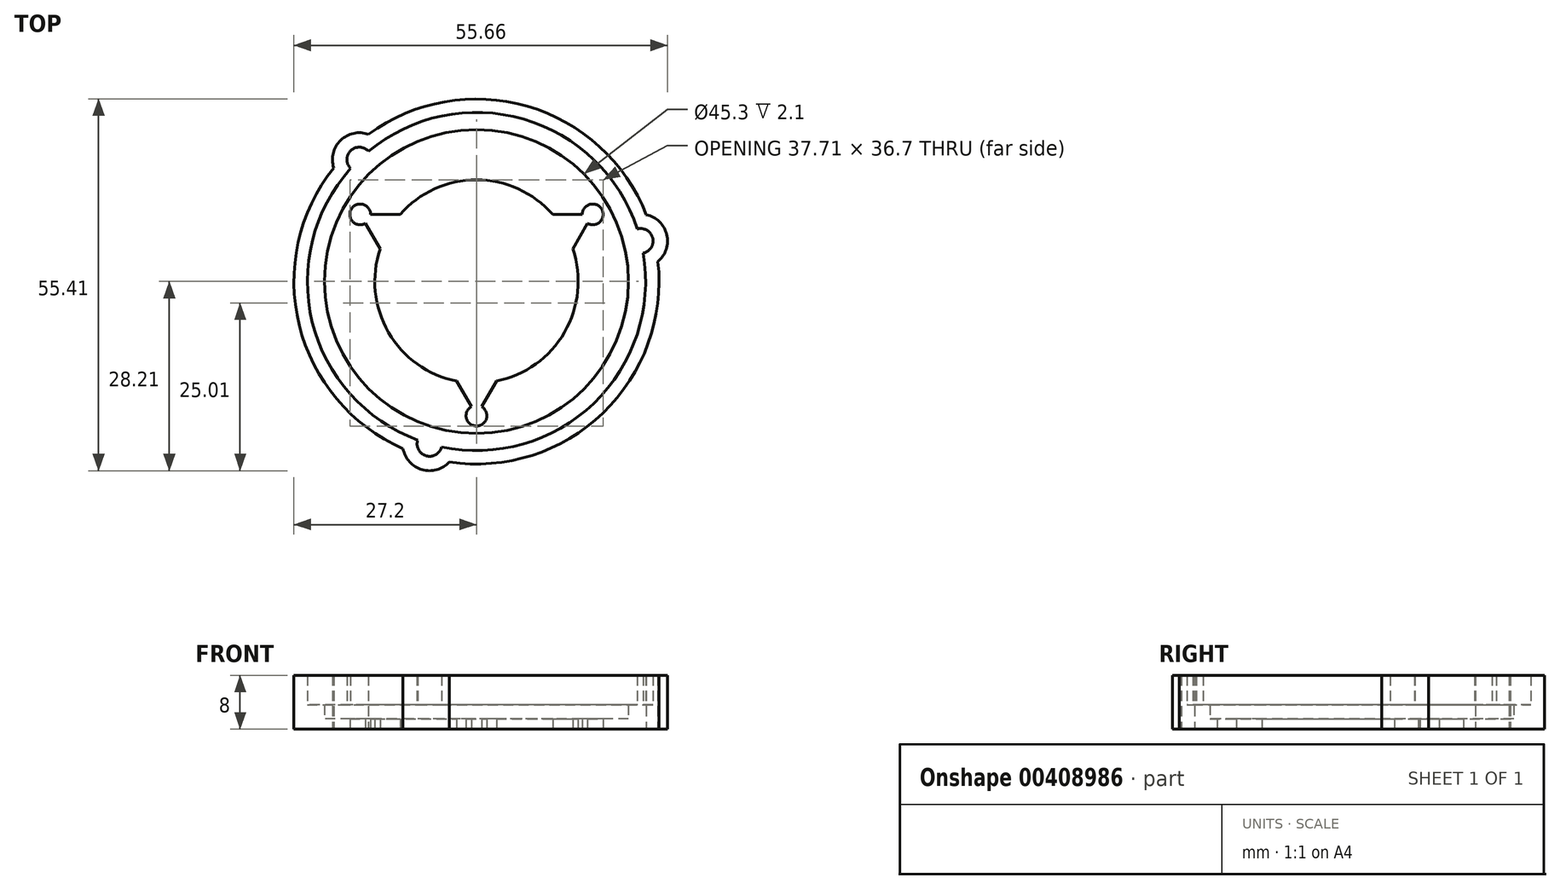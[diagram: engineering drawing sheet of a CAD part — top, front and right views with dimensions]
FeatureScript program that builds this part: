
annotation { "Feature Type Name" : "Feature", "Feature Type Description" : "" }
export const myFeature = defineFeature(function(context is Context, id is Id, definition is map)
    precondition{}
    {
        {
            var Q0;
            Q0=qCreatedBy(makeId("Top.planeOp"),FACE);
            var sketch = newSketch(context, id + "F0", { "sketchPlane" : qUnion([Q0])});
            skCircle(sketch, "E0", {"center": v(0, 0) * mm, "radius": 20 * mm});
            skCircle(sketch, "E1.cCircle", {"center": v(0, 0) * mm, "radius": 20 * mm, "construction": true});
            skCircle(sketch, "E2", {"center": v(0, 0) * mm, "radius": 15.15 * mm});
            skCircle(sketch, "E3", {"center": v(0, 0) * mm, "radius": 0.8 * mm});
            skCircle(sketch, "E4", {"center": v(0, 0) * mm, "radius": 22.65 * mm});
            skCircle(sketch, "E5", {"center": v(0, 0) * mm, "radius": 25.2 * mm});
            skCircle(sketch, "E6", {"center": v(0, 0) * mm, "radius": 27.2 * mm});
            skLineSegment(sketch, "E7.0", {"start": v(0, -20) * mm, "end": v(-17.32, 10) * mm});
            skLineSegment(sketch, "E7.1", {"start": v(-17.32, 10) * mm, "end": v(17.32, 10) * mm});
            skLineSegment(sketch, "E7.2", {"start": v(17.32, 10) * mm, "end": v(0, -20) * mm});
            skCircle(sketch, "E8", {"center": v(-17.32, 10) * mm, "radius": 1.55 * mm});
            skCircle(sketch, "E9", {"center": v(0, -20) * mm, "radius": 1.55 * mm});
            skCircle(sketch, "E10", {"center": v(17.32, 10) * mm, "radius": 1.55 * mm});
            skPoint(sketch, "E11", {"position": v(0, -25.2) * mm});
            skCircle(sketch, "E12.cCircle", {"center": v(0, 0) * mm, "radius": 25.2 * mm, "construction": true});
            skLineSegment(sketch, "E12.0", {"start": v(-7, -24.2) * mm, "end": v(-17.46, 18.17) * mm});
            skLineSegment(sketch, "E12.1", {"start": v(-17.46, 18.17) * mm, "end": v(24.46, 6.04) * mm});
            skLineSegment(sketch, "E12.2", {"start": v(24.46, 6.04) * mm, "end": v(-7, -24.2) * mm});
            skCircle(sketch, "E13", {"center": v(-17.46, 18.17) * mm, "radius": 1.85 * mm});
            skCircle(sketch, "E14", {"center": v(-17.46, 18.17) * mm, "radius": 4 * mm});
            skCircle(sketch, "E15", {"center": v(24.46, 6.04) * mm, "radius": 1.85 * mm});
            skCircle(sketch, "E16", {"center": v(24.46, 6.04) * mm, "radius": 4 * mm});
            skCircle(sketch, "E17", {"center": v(-7, -24.2) * mm, "radius": 1.85 * mm});
            skCircle(sketch, "E18", {"center": v(-7, -24.2) * mm, "radius": 4 * mm});
            skSolve(sketch);
        }
        {
            var Q0;
            Q0 = qSketchRegion(id + "F0", true);
            extrude(context, id + "F1", {"entities" : qUnion([Q0]), "depth" : 8 * mm});
        }
        {
            var Q0;
            {var subQ0=sQuery(id+"F0.wireOp",EDGE,"E14");var subQ1=sQuery(id+"F0.wireOp",EDGE,"E4");var subQ2=makeQuery(id+"F0.imprint","INTERSECT",VERTEX,{"disambiguationData":[OD(1.0)],"derivedFrom":[subQ1,subQ0]});Q0=makeQuery(id+"F0.imprint","IMPRINT",FACE,{"disambiguationData":[TD([[makeQuery(id+"F0.imprint","IMPRINT",EDGE,{"disambiguationData":[TD([[subQ2,-1.0]])],"derivedFrom":subQ1}),-1.0]])]});}
            var Q1;
            {var subQ0=sQuery(id+"F0.wireOp",EDGE,"E12.0");var subQ1=sQuery(id+"F0.wireOp",EDGE,"E4");var subQ2=makeQuery(id+"F0.imprint","INTERSECT",VERTEX,{"disambiguationData":[OD(0.0)],"derivedFrom":[subQ1,subQ0]});Q1=makeQuery(id+"F0.imprint","IMPRINT",FACE,{"disambiguationData":[TD([[makeQuery(id+"F0.imprint","IMPRINT",EDGE,{"disambiguationData":[TD([[subQ2,-1.0]])],"derivedFrom":subQ1}),-1.0]])]});}
            var Q2;
            {var subQ5=sQuery(id+"F0.wireOp",EDGE,"E4");var subQ7=sQuery(id+"F0.wireOp",EDGE,"E14");var subQ9=makeQuery(id+"F0.imprint","INTERSECT",VERTEX,{"disambiguationData":[OD(0.0)],"derivedFrom":[subQ5,subQ7]});Q2=makeQuery(id+"F0.imprint","IMPRINT",FACE,{"disambiguationData":[TD([[makeQuery(id+"F0.imprint","IMPRINT",EDGE,{"disambiguationData":[TD([[subQ9,-1.0]])],"derivedFrom":subQ5}),-1.0]])]});}
            var Q3;
            {var subQ0=sQuery(id+"F0.wireOp",EDGE,"E12.1");var subQ1=sQuery(id+"F0.wireOp",EDGE,"E4");var subQ2=makeQuery(id+"F0.imprint","INTERSECT",VERTEX,{"disambiguationData":[OD(1.0)],"derivedFrom":[subQ1,subQ0]});Q3=makeQuery(id+"F0.imprint","IMPRINT",FACE,{"disambiguationData":[TD([[makeQuery(id+"F0.imprint","IMPRINT",EDGE,{"disambiguationData":[TD([[subQ2,-1.0]])],"derivedFrom":subQ1}),-1.0]])]});}
            var Q4;
            {var subQ1=sQuery(id+"F0.wireOp",EDGE,"E12.0");var subQ3=sQuery(id+"F0.wireOp",EDGE,"E13");var subQ4=makeQuery(id+"F0.imprint","INTERSECT",VERTEX,{"derivedFrom":[subQ1,subQ3]});Q4=makeQuery(id+"F0.imprint","IMPRINT",FACE,{"disambiguationData":[TD([[makeQuery(id+"F0.imprint","IMPRINT",EDGE,{"disambiguationData":[TD([[subQ4,-1.0]])],"derivedFrom":subQ3}),1.0]])]});}
            var Q5;
            {var subQ1=sQuery(id+"F0.wireOp",EDGE,"E5");var subQ3=sQuery(id+"F0.wireOp",EDGE,"E13");var subQ4=makeQuery(id+"F0.imprint","INTERSECT",VERTEX,{"disambiguationData":[OD(1.0)],"derivedFrom":[subQ1,subQ3]});Q5=makeQuery(id+"F0.imprint","IMPRINT",FACE,{"disambiguationData":[TD([[makeQuery(id+"F0.imprint","IMPRINT",EDGE,{"disambiguationData":[TD([[subQ4,-1.0]])],"derivedFrom":subQ3}),1.0]])]});}
            var Q6;
            {var subQ1=sQuery(id+"F0.wireOp",EDGE,"E5");var subQ3=sQuery(id+"F0.wireOp",EDGE,"E13");var subQ4=makeQuery(id+"F0.imprint","INTERSECT",VERTEX,{"disambiguationData":[OD(0.0)],"derivedFrom":[subQ1,subQ3]});Q6=makeQuery(id+"F0.imprint","IMPRINT",FACE,{"disambiguationData":[TD([[makeQuery(id+"F0.imprint","IMPRINT",EDGE,{"disambiguationData":[TD([[subQ4,1.0]])],"derivedFrom":subQ3}),1.0]])]});}
            var Q7;
            {var subQ0=sQuery(id+"F0.wireOp",EDGE,"E5");var subQ2=sQuery(id+"F0.wireOp",EDGE,"E13");var subQ3=makeQuery(id+"F0.imprint","INTERSECT",VERTEX,{"disambiguationData":[OD(0.0)],"derivedFrom":[subQ0,subQ2]});Q7=makeQuery(id+"F0.imprint","IMPRINT",FACE,{"disambiguationData":[TD([[makeQuery(id+"F0.imprint","IMPRINT",EDGE,{"disambiguationData":[TD([[subQ3,-1.0]])],"derivedFrom":subQ2}),1.0]])]});}
            var Q8;
            {var subQ0=sQuery(id+"F0.wireOp",EDGE,"E16");var subQ1=sQuery(id+"F0.wireOp",EDGE,"E4");var subQ2=makeQuery(id+"F0.imprint","INTERSECT",VERTEX,{"disambiguationData":[OD(1.0)],"derivedFrom":[subQ1,subQ0]});Q8=makeQuery(id+"F0.imprint","IMPRINT",FACE,{"disambiguationData":[TD([[makeQuery(id+"F0.imprint","IMPRINT",EDGE,{"disambiguationData":[TD([[subQ2,-1.0]])],"derivedFrom":subQ1}),-1.0]])]});}
            var Q9;
            {var subQ0=sQuery(id+"F0.wireOp",EDGE,"E12.1");var subQ1=sQuery(id+"F0.wireOp",EDGE,"E4");var subQ2=makeQuery(id+"F0.imprint","INTERSECT",VERTEX,{"disambiguationData":[OD(0.0)],"derivedFrom":[subQ1,subQ0]});Q9=makeQuery(id+"F0.imprint","IMPRINT",FACE,{"disambiguationData":[TD([[makeQuery(id+"F0.imprint","IMPRINT",EDGE,{"disambiguationData":[TD([[subQ2,-1.0]])],"derivedFrom":subQ1}),-1.0]])]});}
            var Q10;
            {var subQ1=sQuery(id+"F0.wireOp",EDGE,"E5");var subQ3=sQuery(id+"F0.wireOp",EDGE,"E15");var subQ4=makeQuery(id+"F0.imprint","INTERSECT",VERTEX,{"disambiguationData":[OD(1.0)],"derivedFrom":[subQ1,subQ3]});Q10=makeQuery(id+"F0.imprint","IMPRINT",FACE,{"disambiguationData":[TD([[makeQuery(id+"F0.imprint","IMPRINT",EDGE,{"disambiguationData":[TD([[subQ4,-1.0]])],"derivedFrom":subQ3}),1.0]])]});}
            var Q11;
            {var subQ1=sQuery(id+"F0.wireOp",EDGE,"E12.1");var subQ3=sQuery(id+"F0.wireOp",EDGE,"E15");var subQ4=makeQuery(id+"F0.imprint","INTERSECT",VERTEX,{"derivedFrom":[subQ1,subQ3]});Q11=makeQuery(id+"F0.imprint","IMPRINT",FACE,{"disambiguationData":[TD([[makeQuery(id+"F0.imprint","IMPRINT",EDGE,{"disambiguationData":[TD([[subQ4,-1.0]])],"derivedFrom":subQ3}),1.0]])]});}
            var Q12;
            {var subQ0=sQuery(id+"F0.wireOp",EDGE,"E5");var subQ2=sQuery(id+"F0.wireOp",EDGE,"E15");var subQ3=makeQuery(id+"F0.imprint","INTERSECT",VERTEX,{"disambiguationData":[OD(0.0)],"derivedFrom":[subQ0,subQ2]});Q12=makeQuery(id+"F0.imprint","IMPRINT",FACE,{"disambiguationData":[TD([[makeQuery(id+"F0.imprint","IMPRINT",EDGE,{"disambiguationData":[TD([[subQ3,-1.0]])],"derivedFrom":subQ2}),1.0]])]});}
            var Q13;
            {var subQ0=sQuery(id+"F0.wireOp",EDGE,"E12.2");var subQ1=sQuery(id+"F0.wireOp",EDGE,"E4");var subQ2=makeQuery(id+"F0.imprint","INTERSECT",VERTEX,{"disambiguationData":[OD(0.0)],"derivedFrom":[subQ1,subQ0]});Q13=makeQuery(id+"F0.imprint","IMPRINT",FACE,{"disambiguationData":[TD([[makeQuery(id+"F0.imprint","IMPRINT",EDGE,{"disambiguationData":[TD([[subQ2,-1.0]])],"derivedFrom":subQ1}),-1.0]])]});}
            var Q14;
            {var subQ1=sQuery(id+"F0.wireOp",EDGE,"E5");var subQ3=sQuery(id+"F0.wireOp",EDGE,"E15");var subQ4=makeQuery(id+"F0.imprint","INTERSECT",VERTEX,{"disambiguationData":[OD(0.0)],"derivedFrom":[subQ1,subQ3]});Q14=makeQuery(id+"F0.imprint","IMPRINT",FACE,{"disambiguationData":[TD([[makeQuery(id+"F0.imprint","IMPRINT",EDGE,{"disambiguationData":[TD([[subQ4,1.0]])],"derivedFrom":subQ3}),1.0]])]});}
            var Q15;
            {var subQ3=sQuery(id+"F0.wireOp",EDGE,"E12.2");var subQ5=sQuery(id+"F0.wireOp",EDGE,"E4");var subQ6=makeQuery(id+"F0.imprint","INTERSECT",VERTEX,{"disambiguationData":[OD(0.0)],"derivedFrom":[subQ5,subQ3]});Q15=makeQuery(id+"F0.imprint","IMPRINT",FACE,{"disambiguationData":[TD([[makeQuery(id+"F0.imprint","IMPRINT",EDGE,{"disambiguationData":[TD([[subQ6,1.0]])],"derivedFrom":subQ5}),-1.0]])]});}
            var Q16;
            {var subQ0=sQuery(id+"F0.wireOp",EDGE,"E16");var subQ1=sQuery(id+"F0.wireOp",EDGE,"E4");var subQ2=makeQuery(id+"F0.imprint","INTERSECT",VERTEX,{"disambiguationData":[OD(0.0)],"derivedFrom":[subQ1,subQ0]});Q16=makeQuery(id+"F0.imprint","IMPRINT",FACE,{"disambiguationData":[TD([[makeQuery(id+"F0.imprint","IMPRINT",EDGE,{"disambiguationData":[TD([[subQ2,1.0]])],"derivedFrom":subQ1}),-1.0]])]});}
            var Q17;
            {var subQ3=sQuery(id+"F0.wireOp",EDGE,"E12.2");var subQ5=sQuery(id+"F0.wireOp",EDGE,"E4");var subQ6=makeQuery(id+"F0.imprint","INTERSECT",VERTEX,{"disambiguationData":[OD(1.0)],"derivedFrom":[subQ5,subQ3]});Q17=makeQuery(id+"F0.imprint","IMPRINT",FACE,{"disambiguationData":[TD([[makeQuery(id+"F0.imprint","IMPRINT",EDGE,{"disambiguationData":[TD([[subQ6,-1.0]])],"derivedFrom":subQ5}),-1.0]])]});}
            var Q18;
            {var subQ0=sQuery(id+"F0.wireOp",EDGE,"E12.0");var subQ1=sQuery(id+"F0.wireOp",EDGE,"E4");var subQ2=makeQuery(id+"F0.imprint","INTERSECT",VERTEX,{"disambiguationData":[OD(1.0)],"derivedFrom":[subQ1,subQ0]});Q18=makeQuery(id+"F0.imprint","IMPRINT",FACE,{"disambiguationData":[TD([[makeQuery(id+"F0.imprint","IMPRINT",EDGE,{"disambiguationData":[TD([[subQ2,-1.0]])],"derivedFrom":subQ1}),-1.0]])]});}
            var Q19;
            {var subQ5=sQuery(id+"F0.wireOp",EDGE,"E4");var subQ7=sQuery(id+"F0.wireOp",EDGE,"E18");var subQ9=makeQuery(id+"F0.imprint","INTERSECT",VERTEX,{"disambiguationData":[OD(0.0)],"derivedFrom":[subQ5,subQ7]});Q19=makeQuery(id+"F0.imprint","IMPRINT",FACE,{"disambiguationData":[TD([[makeQuery(id+"F0.imprint","IMPRINT",EDGE,{"disambiguationData":[TD([[subQ9,-1.0]])],"derivedFrom":subQ5}),-1.0]])]});}
            var Q20;
            {var subQ1=sQuery(id+"F0.wireOp",EDGE,"E5");var subQ3=sQuery(id+"F0.wireOp",EDGE,"E17");var subQ4=makeQuery(id+"F0.imprint","INTERSECT",VERTEX,{"disambiguationData":[OD(0.0)],"derivedFrom":[subQ1,subQ3]});Q20=makeQuery(id+"F0.imprint","IMPRINT",FACE,{"disambiguationData":[TD([[makeQuery(id+"F0.imprint","IMPRINT",EDGE,{"disambiguationData":[TD([[subQ4,1.0]])],"derivedFrom":subQ3}),1.0]])]});}
            var Q21;
            {var subQ1=sQuery(id+"F0.wireOp",EDGE,"E12.0");var subQ3=sQuery(id+"F0.wireOp",EDGE,"E17");var subQ4=makeQuery(id+"F0.imprint","INTERSECT",VERTEX,{"derivedFrom":[subQ1,subQ3]});Q21=makeQuery(id+"F0.imprint","IMPRINT",FACE,{"disambiguationData":[TD([[makeQuery(id+"F0.imprint","IMPRINT",EDGE,{"disambiguationData":[TD([[subQ4,1.0]])],"derivedFrom":subQ3}),1.0]])]});}
            var Q22;
            {var subQ1=sQuery(id+"F0.wireOp",EDGE,"E5");var subQ3=sQuery(id+"F0.wireOp",EDGE,"E17");var subQ4=makeQuery(id+"F0.imprint","INTERSECT",VERTEX,{"disambiguationData":[OD(1.0)],"derivedFrom":[subQ1,subQ3]});Q22=makeQuery(id+"F0.imprint","IMPRINT",FACE,{"disambiguationData":[TD([[makeQuery(id+"F0.imprint","IMPRINT",EDGE,{"disambiguationData":[TD([[subQ4,-1.0]])],"derivedFrom":subQ3}),1.0]])]});}
            var Q23;
            {var subQ0=sQuery(id+"F0.wireOp",EDGE,"E5");var subQ2=sQuery(id+"F0.wireOp",EDGE,"E17");var subQ3=makeQuery(id+"F0.imprint","INTERSECT",VERTEX,{"disambiguationData":[OD(0.0)],"derivedFrom":[subQ0,subQ2]});Q23=makeQuery(id+"F0.imprint","IMPRINT",FACE,{"disambiguationData":[TD([[makeQuery(id+"F0.imprint","IMPRINT",EDGE,{"disambiguationData":[TD([[subQ3,-1.0]])],"derivedFrom":subQ2}),1.0]])]});}
            extrude(context, id + "F2", {"entities" : qUnion([Q0, Q1, Q2, Q3, Q4, Q5, Q6, Q7, Q8, Q9, Q10, Q11, Q12, Q13, Q14, Q15, Q16, Q17, Q18, Q19, Q20, Q21, Q22, Q23]), "operationType" : NewBodyOperationType.ADD, "depth" : 3.6 * mm});
        }
        {
            var Q0;
            Q0 = qSketchRegion(id + "F0", true);
            var Q1;
            {var subQ0=sQuery(id+"F0.wireOp",EDGE,"E12.0");var subQ1=sQuery(id+"F0.wireOp",EDGE,"E4");var subQ2=makeQuery(id+"F0.imprint","INTERSECT",VERTEX,{"disambiguationData":[OD(0.0)],"derivedFrom":[subQ1,subQ0]});Q1=makeQuery(id+"F0.imprint","IMPRINT",FACE,{"disambiguationData":[TD([[makeQuery(id+"F0.imprint","IMPRINT",EDGE,{"disambiguationData":[TD([[subQ2,-1.0]])],"derivedFrom":subQ1}),1.0]])]});}
            var Q2;
            {var subQ0=sQuery(id+"F0.wireOp",EDGE,"E12.1");var subQ1=sQuery(id+"F0.wireOp",EDGE,"E4");var subQ2=makeQuery(id+"F0.imprint","INTERSECT",VERTEX,{"disambiguationData":[OD(1.0)],"derivedFrom":[subQ1,subQ0]});Q2=makeQuery(id+"F0.imprint","IMPRINT",FACE,{"disambiguationData":[TD([[makeQuery(id+"F0.imprint","IMPRINT",EDGE,{"disambiguationData":[TD([[subQ2,-1.0]])],"derivedFrom":subQ1}),1.0]])]});}
            var Q3;
            {var subQ0=sQuery(id+"F0.wireOp",EDGE,"E14");var subQ1=sQuery(id+"F0.wireOp",EDGE,"E4");var subQ2=makeQuery(id+"F0.imprint","INTERSECT",VERTEX,{"disambiguationData":[OD(0.0)],"derivedFrom":[subQ1,subQ0]});Q3=makeQuery(id+"F0.imprint","IMPRINT",FACE,{"disambiguationData":[TD([[makeQuery(id+"F0.imprint","IMPRINT",EDGE,{"disambiguationData":[TD([[subQ2,-1.0]])],"derivedFrom":subQ1}),1.0]])]});}
            var Q4;
            {var subQ1=sQuery(id+"F0.wireOp",EDGE,"E0");var subQ4=sQuery(id+"F0.wireOp",EDGE,"E12.1");var subQ11=makeQuery(id+"F0.imprint","INTERSECT",VERTEX,{"disambiguationData":[OD(0.0)],"derivedFrom":[subQ1,subQ4]});Q4=makeQuery(id+"F0.imprint","IMPRINT",FACE,{"disambiguationData":[TD([[makeQuery(id+"F0.imprint","IMPRINT",EDGE,{"disambiguationData":[TD([[subQ11,-1.0]])],"derivedFrom":subQ1}),-1.0]])]});}
            var Q5;
            {var subQ0=sQuery(id+"F0.wireOp",EDGE,"E12.1");var subQ1=sQuery(id+"F0.wireOp",EDGE,"E0");var subQ2=makeQuery(id+"F0.imprint","INTERSECT",VERTEX,{"disambiguationData":[OD(1.0)],"derivedFrom":[subQ1,subQ0]});Q5=makeQuery(id+"F0.imprint","IMPRINT",FACE,{"disambiguationData":[TD([[makeQuery(id+"F0.imprint","IMPRINT",EDGE,{"disambiguationData":[TD([[subQ2,-1.0]])],"derivedFrom":subQ1}),-1.0]])]});}
            var Q6;
            {var subQ1=sQuery(id+"F0.wireOp",EDGE,"E0");var subQ4=sQuery(id+"F0.wireOp",EDGE,"E12.0");var subQ5=makeQuery(id+"F0.imprint","INTERSECT",VERTEX,{"disambiguationData":[OD(0.0)],"derivedFrom":[subQ1,subQ4]});Q6=makeQuery(id+"F0.imprint","IMPRINT",FACE,{"disambiguationData":[TD([[makeQuery(id+"F0.imprint","IMPRINT",EDGE,{"disambiguationData":[TD([[subQ5,-1.0]])],"derivedFrom":subQ1}),-1.0]])]});}
            var Q7;
            {var subQ3=sQuery(id+"F0.wireOp",EDGE,"E8");var subQ7=sQuery(id+"F0.wireOp",EDGE,"E0");var subQ9=makeQuery(id+"F0.imprint","INTERSECT",VERTEX,{"disambiguationData":[OD(1.0)],"derivedFrom":[subQ7,subQ3]});Q7=makeQuery(id+"F0.imprint","IMPRINT",FACE,{"disambiguationData":[TD([[makeQuery(id+"F0.imprint","IMPRINT",EDGE,{"disambiguationData":[TD([[subQ9,-1.0]])],"derivedFrom":subQ7}),1.0]])]});}
            var Q8;
            {var subQ3=sQuery(id+"F0.wireOp",EDGE,"E12.0");var subQ6=sQuery(id+"F0.wireOp",EDGE,"E2");var subQ9=makeQuery(id+"F0.imprint","INTERSECT",VERTEX,{"disambiguationData":[OD(0.0)],"derivedFrom":[subQ6,subQ3]});Q8=makeQuery(id+"F0.imprint","IMPRINT",FACE,{"disambiguationData":[TD([[makeQuery(id+"F0.imprint","IMPRINT",EDGE,{"disambiguationData":[TD([[subQ9,-1.0]])],"derivedFrom":subQ6}),-1.0]])]});}
            var Q9;
            {var subQ0=sQuery(id+"F0.wireOp",EDGE,"E12.0");var subQ1=sQuery(id+"F0.wireOp",EDGE,"E0");var subQ2=makeQuery(id+"F0.imprint","INTERSECT",VERTEX,{"disambiguationData":[OD(0.0)],"derivedFrom":[subQ1,subQ0]});Q9=makeQuery(id+"F0.imprint","IMPRINT",FACE,{"disambiguationData":[TD([[makeQuery(id+"F0.imprint","IMPRINT",EDGE,{"disambiguationData":[TD([[subQ2,-1.0]])],"derivedFrom":subQ1}),1.0]])]});}
            var Q10;
            {var subQ1=sQuery(id+"F0.wireOp",EDGE,"E0");var subQ5=sQuery(id+"F0.wireOp",EDGE,"E12.1");var subQ9=makeQuery(id+"F0.imprint","INTERSECT",VERTEX,{"disambiguationData":[OD(1.0)],"derivedFrom":[subQ1,subQ5]});Q10=makeQuery(id+"F0.imprint","IMPRINT",FACE,{"disambiguationData":[TD([[makeQuery(id+"F0.imprint","IMPRINT",EDGE,{"disambiguationData":[TD([[subQ9,-1.0]])],"derivedFrom":subQ1}),1.0]])]});}
            var Q11;
            {var subQ0=sQuery(id+"F0.wireOp",EDGE,"E7.1");var subQ1=sQuery(id+"F0.wireOp",EDGE,"E2");var subQ2=makeQuery(id+"F0.imprint","INTERSECT",VERTEX,{"disambiguationData":[OD(1.0)],"derivedFrom":[subQ1,subQ0]});Q11=makeQuery(id+"F0.imprint","IMPRINT",FACE,{"disambiguationData":[TD([[makeQuery(id+"F0.imprint","IMPRINT",EDGE,{"disambiguationData":[TD([[subQ2,-1.0]])],"derivedFrom":subQ1}),-1.0]])]});}
            var Q12;
            {var subQ0=sQuery(id+"F0.wireOp",EDGE,"E10");var subQ1=sQuery(id+"F0.wireOp",EDGE,"E0");var subQ2=makeQuery(id+"F0.imprint","INTERSECT",VERTEX,{"disambiguationData":[OD(1.0)],"derivedFrom":[subQ1,subQ0]});Q12=makeQuery(id+"F0.imprint","IMPRINT",FACE,{"disambiguationData":[TD([[makeQuery(id+"F0.imprint","IMPRINT",EDGE,{"disambiguationData":[TD([[subQ2,-1.0]])],"derivedFrom":subQ1}),1.0]])]});}
            var Q13;
            {var subQ1=sQuery(id+"F0.wireOp",EDGE,"E2");var subQ7=sQuery(id+"F0.wireOp",EDGE,"E12.1");var subQ9=makeQuery(id+"F0.imprint","INTERSECT",VERTEX,{"disambiguationData":[OD(0.0)],"derivedFrom":[subQ1,subQ7]});Q13=makeQuery(id+"F0.imprint","IMPRINT",FACE,{"disambiguationData":[TD([[makeQuery(id+"F0.imprint","IMPRINT",EDGE,{"disambiguationData":[TD([[subQ9,-1.0]])],"derivedFrom":subQ1}),-1.0]])]});}
            var Q14;
            {var subQ0=sQuery(id+"F0.wireOp",EDGE,"E12.1");var subQ1=sQuery(id+"F0.wireOp",EDGE,"E0");var subQ2=makeQuery(id+"F0.imprint","INTERSECT",VERTEX,{"disambiguationData":[OD(0.0)],"derivedFrom":[subQ1,subQ0]});Q14=makeQuery(id+"F0.imprint","IMPRINT",FACE,{"disambiguationData":[TD([[makeQuery(id+"F0.imprint","IMPRINT",EDGE,{"disambiguationData":[TD([[subQ2,-1.0]])],"derivedFrom":subQ1}),1.0]])]});}
            var Q15;
            {var subQ3=sQuery(id+"F0.wireOp",EDGE,"E12.1");var subQ5=sQuery(id+"F0.wireOp",EDGE,"E0");var subQ6=makeQuery(id+"F0.imprint","INTERSECT",VERTEX,{"disambiguationData":[OD(0.0)],"derivedFrom":[subQ5,subQ3]});Q15=makeQuery(id+"F0.imprint","IMPRINT",FACE,{"disambiguationData":[TD([[makeQuery(id+"F0.imprint","IMPRINT",EDGE,{"disambiguationData":[TD([[subQ6,1.0]])],"derivedFrom":subQ5}),1.0]])]});}
            var Q16;
            {var subQ0=sQuery(id+"F0.wireOp",EDGE,"E12.1");var subQ1=sQuery(id+"F0.wireOp",EDGE,"E2");var subQ2=makeQuery(id+"F0.imprint","INTERSECT",VERTEX,{"disambiguationData":[OD(0.0)],"derivedFrom":[subQ1,subQ0]});Q16=makeQuery(id+"F0.imprint","IMPRINT",FACE,{"disambiguationData":[TD([[makeQuery(id+"F0.imprint","IMPRINT",EDGE,{"disambiguationData":[TD([[subQ2,1.0]])],"derivedFrom":subQ1}),-1.0]])]});}
            var Q17;
            {var subQ0=sQuery(id+"F0.wireOp",EDGE,"E12.1");var subQ1=sQuery(id+"F0.wireOp",EDGE,"E4");var subQ2=makeQuery(id+"F0.imprint","INTERSECT",VERTEX,{"disambiguationData":[OD(0.0)],"derivedFrom":[subQ1,subQ0]});Q17=makeQuery(id+"F0.imprint","IMPRINT",FACE,{"disambiguationData":[TD([[makeQuery(id+"F0.imprint","IMPRINT",EDGE,{"disambiguationData":[TD([[subQ2,-1.0]])],"derivedFrom":subQ1}),1.0]])]});}
            var Q18;
            {var subQ0=sQuery(id+"F0.wireOp",EDGE,"E12.2");var subQ1=sQuery(id+"F0.wireOp",EDGE,"E4");var subQ2=makeQuery(id+"F0.imprint","INTERSECT",VERTEX,{"disambiguationData":[OD(0.0)],"derivedFrom":[subQ1,subQ0]});Q18=makeQuery(id+"F0.imprint","IMPRINT",FACE,{"disambiguationData":[TD([[makeQuery(id+"F0.imprint","IMPRINT",EDGE,{"disambiguationData":[TD([[subQ2,-1.0]])],"derivedFrom":subQ1}),1.0]])]});}
            var Q19;
            {var subQ0=sQuery(id+"F0.wireOp",EDGE,"E12.2");var subQ1=sQuery(id+"F0.wireOp",EDGE,"E4");var subQ2=makeQuery(id+"F0.imprint","INTERSECT",VERTEX,{"disambiguationData":[OD(0.0)],"derivedFrom":[subQ1,subQ0]});Q19=makeQuery(id+"F0.imprint","IMPRINT",FACE,{"disambiguationData":[TD([[makeQuery(id+"F0.imprint","IMPRINT",EDGE,{"disambiguationData":[TD([[subQ2,1.0]])],"derivedFrom":subQ1}),1.0]])]});}
            var Q20;
            {var subQ1=sQuery(id+"F0.wireOp",EDGE,"E0");var subQ9=sQuery(id+"F0.wireOp",EDGE,"E12.2");var subQ11=makeQuery(id+"F0.imprint","INTERSECT",VERTEX,{"disambiguationData":[OD(1.0)],"derivedFrom":[subQ1,subQ9]});Q20=makeQuery(id+"F0.imprint","IMPRINT",FACE,{"disambiguationData":[TD([[makeQuery(id+"F0.imprint","IMPRINT",EDGE,{"disambiguationData":[TD([[subQ11,-1.0]])],"derivedFrom":subQ1}),-1.0]])]});}
            var Q21;
            {var subQ0=sQuery(id+"F0.wireOp",EDGE,"E12.1");var subQ1=sQuery(id+"F0.wireOp",EDGE,"E0");var subQ2=makeQuery(id+"F0.imprint","INTERSECT",VERTEX,{"disambiguationData":[OD(0.0)],"derivedFrom":[subQ1,subQ0]});Q21=makeQuery(id+"F0.imprint","IMPRINT",FACE,{"disambiguationData":[TD([[makeQuery(id+"F0.imprint","IMPRINT",EDGE,{"disambiguationData":[TD([[subQ2,1.0]])],"derivedFrom":subQ1}),-1.0]])]});}
            var Q22;
            {var subQ1=sQuery(id+"F0.wireOp",EDGE,"E0");var subQ7=sQuery(id+"F0.wireOp",EDGE,"E12.2");var subQ9=makeQuery(id+"F0.imprint","INTERSECT",VERTEX,{"disambiguationData":[OD(0.0)],"derivedFrom":[subQ1,subQ7]});Q22=makeQuery(id+"F0.imprint","IMPRINT",FACE,{"disambiguationData":[TD([[makeQuery(id+"F0.imprint","IMPRINT",EDGE,{"disambiguationData":[TD([[subQ9,1.0]])],"derivedFrom":subQ1}),1.0]])]});}
            var Q23;
            {var subQ0=sQuery(id+"F0.wireOp",EDGE,"E18");var subQ1=sQuery(id+"F0.wireOp",EDGE,"E4");var subQ2=makeQuery(id+"F0.imprint","INTERSECT",VERTEX,{"disambiguationData":[OD(0.0)],"derivedFrom":[subQ1,subQ0]});Q23=makeQuery(id+"F0.imprint","IMPRINT",FACE,{"disambiguationData":[TD([[makeQuery(id+"F0.imprint","IMPRINT",EDGE,{"disambiguationData":[TD([[subQ2,-1.0]])],"derivedFrom":subQ1}),1.0]])]});}
            var Q24;
            {var subQ0=sQuery(id+"F0.wireOp",EDGE,"E12.0");var subQ1=sQuery(id+"F0.wireOp",EDGE,"E4");var subQ2=makeQuery(id+"F0.imprint","INTERSECT",VERTEX,{"disambiguationData":[OD(1.0)],"derivedFrom":[subQ1,subQ0]});Q24=makeQuery(id+"F0.imprint","IMPRINT",FACE,{"disambiguationData":[TD([[makeQuery(id+"F0.imprint","IMPRINT",EDGE,{"disambiguationData":[TD([[subQ2,-1.0]])],"derivedFrom":subQ1}),1.0]])]});}
            var Q25;
            {var subQ0=sQuery(id+"F0.wireOp",EDGE,"E12.2");var subQ1=sQuery(id+"F0.wireOp",EDGE,"E4");var subQ2=makeQuery(id+"F0.imprint","INTERSECT",VERTEX,{"disambiguationData":[OD(1.0)],"derivedFrom":[subQ1,subQ0]});Q25=makeQuery(id+"F0.imprint","IMPRINT",FACE,{"disambiguationData":[TD([[makeQuery(id+"F0.imprint","IMPRINT",EDGE,{"disambiguationData":[TD([[subQ2,-1.0]])],"derivedFrom":subQ1}),1.0]])]});}
            var Q26;
            {var subQ0=sQuery(id+"F0.wireOp",EDGE,"E12.2");var subQ1=sQuery(id+"F0.wireOp",EDGE,"E0");var subQ2=makeQuery(id+"F0.imprint","INTERSECT",VERTEX,{"disambiguationData":[OD(1.0)],"derivedFrom":[subQ1,subQ0]});Q26=makeQuery(id+"F0.imprint","IMPRINT",FACE,{"disambiguationData":[TD([[makeQuery(id+"F0.imprint","IMPRINT",EDGE,{"disambiguationData":[TD([[subQ2,-1.0]])],"derivedFrom":subQ1}),1.0]])]});}
            var Q27;
            {var subQ1=sQuery(id+"F0.wireOp",EDGE,"E2");var subQ7=sQuery(id+"F0.wireOp",EDGE,"E12.2");var subQ9=makeQuery(id+"F0.imprint","INTERSECT",VERTEX,{"disambiguationData":[OD(0.0)],"derivedFrom":[subQ1,subQ7]});Q27=makeQuery(id+"F0.imprint","IMPRINT",FACE,{"disambiguationData":[TD([[makeQuery(id+"F0.imprint","IMPRINT",EDGE,{"disambiguationData":[TD([[subQ9,-1.0]])],"derivedFrom":subQ1}),-1.0]])]});}
            var Q28;
            {var subQ0=sQuery(id+"F0.wireOp",EDGE,"E12.0");var subQ1=sQuery(id+"F0.wireOp",EDGE,"E0");var subQ2=makeQuery(id+"F0.imprint","INTERSECT",VERTEX,{"disambiguationData":[OD(1.0)],"derivedFrom":[subQ1,subQ0]});Q28=makeQuery(id+"F0.imprint","IMPRINT",FACE,{"disambiguationData":[TD([[makeQuery(id+"F0.imprint","IMPRINT",EDGE,{"disambiguationData":[TD([[subQ2,-1.0]])],"derivedFrom":subQ1}),1.0]])]});}
            var Q29;
            {var subQ0=sQuery(id+"F0.wireOp",EDGE,"E7.0");var subQ1=sQuery(id+"F0.wireOp",EDGE,"E2");var subQ2=makeQuery(id+"F0.imprint","INTERSECT",VERTEX,{"disambiguationData":[OD(1.0)],"derivedFrom":[subQ1,subQ0]});Q29=makeQuery(id+"F0.imprint","IMPRINT",FACE,{"disambiguationData":[TD([[makeQuery(id+"F0.imprint","IMPRINT",EDGE,{"disambiguationData":[TD([[subQ2,-1.0]])],"derivedFrom":subQ1}),-1.0]])]});}
            var Q30;
            {var subQ0=sQuery(id+"F0.wireOp",EDGE,"E12.0");var subQ1=sQuery(id+"F0.wireOp",EDGE,"E0");var subQ2=makeQuery(id+"F0.imprint","INTERSECT",VERTEX,{"disambiguationData":[OD(1.0)],"derivedFrom":[subQ1,subQ0]});Q30=makeQuery(id+"F0.imprint","IMPRINT",FACE,{"disambiguationData":[TD([[makeQuery(id+"F0.imprint","IMPRINT",EDGE,{"disambiguationData":[TD([[subQ2,-1.0]])],"derivedFrom":subQ1}),-1.0]])]});}
            extrude(context, id + "F3", {"entities" : qUnion([Q0, Q1, Q2, Q3, Q4, Q5, Q6, Q7, Q8, Q9, Q10, Q11, Q12, Q13, Q14, Q15, Q16, Q17, Q18, Q19, Q20, Q21, Q22, Q23, Q24, Q25, Q26, Q27, Q28, Q29, Q30]), "operationType" : NewBodyOperationType.ADD, "depth" : 1.5 * mm});
        }
    });
